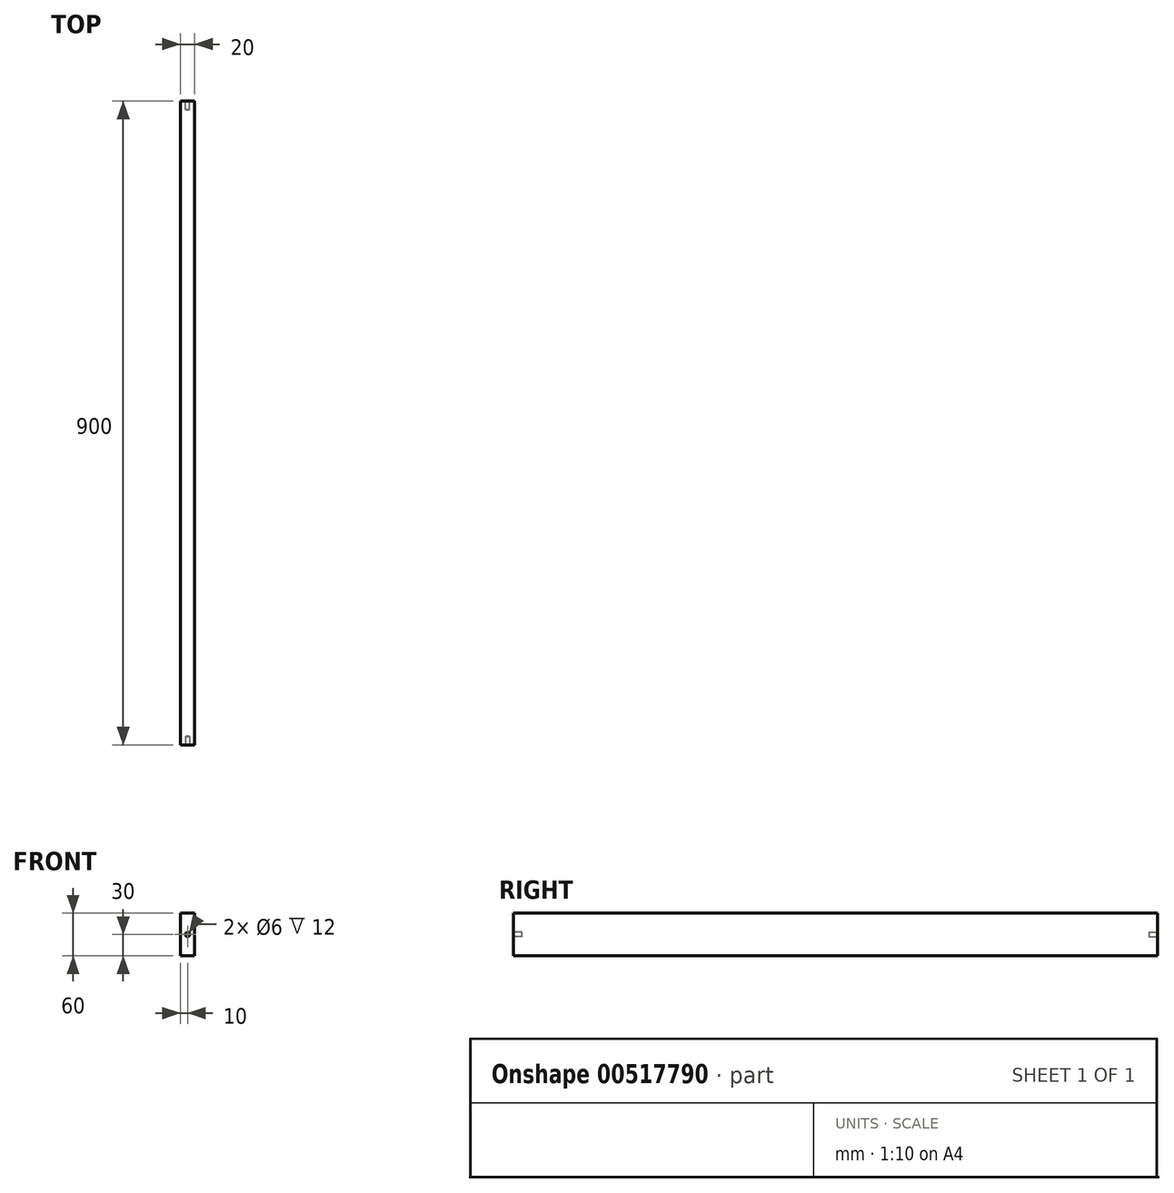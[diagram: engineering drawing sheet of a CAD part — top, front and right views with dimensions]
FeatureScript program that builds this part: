
annotation { "Feature Type Name" : "Feature", "Feature Type Description" : "" }
export const myFeature = defineFeature(function(context is Context, id is Id, definition is map)
    precondition{}
    {
        {
            var Q0;
            Q0=qCreatedBy(makeId("Front.planeOp"),FACE);
            var sketch = newSketch(context, id + "F0", { "sketchPlane" : qUnion([Q0])});
            skLineSegment(sketch, "E0.bottom", {"start": v(0, 0) * mm, "end": v(20, 0) * mm});
            skLineSegment(sketch, "E0.top", {"start": v(0, 60) * mm, "end": v(20, 60) * mm});
            skLineSegment(sketch, "E0.left", {"start": v(0, 0) * mm, "end": v(0, 60) * mm});
            skLineSegment(sketch, "E0.right", {"start": v(20, 0) * mm, "end": v(20, 60) * mm});
            skSolve(sketch);
        }
        {
            var Q0;
            Q0=makeQuery(id+"F0.imprint","IMPRINT",FACE,{"disambiguationData":[TD([[makeQuery(id+"F0.imprint","IMPRINT",EDGE,{"derivedFrom":sQuery(id+"F0.wireOp",EDGE,"E0.bottom")}),1.0]])]});
            extrude(context, id + "F1", {"entities" : qUnion([Q0]), "endBound" : BoundingType.SYMMETRIC, "depth" : 900 * mm, "offsetDistance" : 25 * mm});
        }
        {
            var Q0;
            Q0=makeQuery(id+"F1.opExtrude","CAP_FACE",FACE,{"disambiguationData":[OSD([sQuery(id+"F0.wireOp",EDGE,"E0.bottom"),sQuery(id+"F0.wireOp",EDGE,"E0.top"),sQuery(id+"F0.wireOp",EDGE,"E0.left"),sQuery(id+"F0.wireOp",EDGE,"E0.right")])],"isStart":false});
            var sketch = newSketch(context, id + "F2", { "sketchPlane" : qUnion([Q0])});
            skCircle(sketch, "E1", {"center": v(10, 30) * mm, "radius": 3 * mm});
            skPoint(sketch, "E1.centerSnap0", {"position": v(10, 60) * mm});
            skPoint(sketch, "E1.centerSnap1", {"position": v(0, 30) * mm});
            skSolve(sketch);
        }
        {
            var Q0;
            Q0=makeQuery(id+"F2.imprint","IMPRINT",FACE,{"disambiguationData":[TD([[makeQuery(id+"F2.imprint","IMPRINT",EDGE,{"derivedFrom":sQuery(id+"F2.wireOp",EDGE,"E1")}),1.0]])]});
            var Q1;
            Q1=sQuery(id+"F2.wireOp",EDGE,"E1");
            extrude(context, id + "F3", {"entities" : qUnion([Q0]), "operationType" : NewBodyOperationType.REMOVE, "surfaceEntities" : qUnion([Q1]), "oppositeDirection" : true, "depth" : 12 * mm, "offsetDistance" : 25 * mm});
        }
        {
            var Q0;
            Q0=makeQuery(id+"F1.opExtrude","CAP_FACE",FACE,{"disambiguationData":[OSD([sQuery(id+"F0.wireOp",EDGE,"E0.bottom"),sQuery(id+"F0.wireOp",EDGE,"E0.top"),sQuery(id+"F0.wireOp",EDGE,"E0.left"),sQuery(id+"F0.wireOp",EDGE,"E0.right")])],"isStart":true});
            var sketch = newSketch(context, id + "F4", { "sketchPlane" : qUnion([Q0])});
            skSolve(sketch);
        }
        {
            var Q0;
            Q0=makeQuery(id+"F4.imprint","IMPRINT",FACE,{"disambiguationData":[TD([[makeQuery(id+"F4.imprint","IMPRINT",EDGE,{"derivedFrom":makeQuery(id+"F1.opExtrude","CAP_EDGE",EDGE,{"disambiguationData":[OSD([sQuery(id+"F0.wireOp",EDGE,"E0.bottom")])],"isStart":true})}),-1.0]])]});
            var sketch = newSketch(context, id + "F5", { "sketchPlane" : qUnion([Q0])});
            skLineSegment(sketch, "E2.0.0", {"start": v(-20, 60) * mm, "end": v(0, 60) * mm});
            skLineSegment(sketch, "E2.0.1", {"start": v(0, 60) * mm, "end": v(0, 0) * mm});
            skLineSegment(sketch, "E2.0.2", {"start": v(0, 0) * mm, "end": v(-20, 0) * mm});
            skLineSegment(sketch, "E2.0.3", {"start": v(-20, 0) * mm, "end": v(-20, 60) * mm});
            skCircle(sketch, "E3.0", {"center": v(-10, 30) * mm, "radius": 3 * mm});
            skSolve(sketch);
        }
        {
            var Q0;
            Q0=makeQuery(id+"F5.imprint","IMPRINT",FACE,{"disambiguationData":[TD([[makeQuery(id+"F5.imprint","IMPRINT",EDGE,{"derivedFrom":sQuery(id+"F5.wireOp",EDGE,"E3.0")}),1.0]])]});
            extrude(context, id + "F6", {"entities" : qUnion([Q0]), "operationType" : NewBodyOperationType.REMOVE, "oppositeDirection" : true, "depth" : 12 * mm, "offsetDistance" : 25 * mm});
        }
    });
